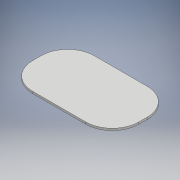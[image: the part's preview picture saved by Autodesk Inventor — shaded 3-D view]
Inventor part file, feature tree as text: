
AUTODESK INVENTOR PART (.ipt)
format: ipt  version: 2018 (Build 220112000, 112)  size: 109,056 bytes
history: native  units: mm
features: extrude x1, sketch x1
ambient origin geometry x8: Origin, YZ Plane, XZ Plane, XY Plane, X Axis, Y Axis, Z Axis, Center Point
bodies: Solid1 (feature_tree)
feature tree (2):
  extrude  "Extrusion1"  Depth=58.0mm
  sketch  "Sketch1"  dims[d0=100.0mm d1=58.0mm d2=25.0mm d3=1.93mm d4=0.0mm]
